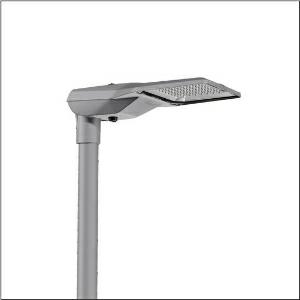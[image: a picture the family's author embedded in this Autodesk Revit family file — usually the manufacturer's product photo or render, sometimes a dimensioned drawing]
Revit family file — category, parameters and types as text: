
# Revit family: streetlight_sl_21_iq_midi___st1_0a_5xe3d61y08nb_32be
name_source: partatom
category: Lighting Fixtures
units: mm (PartAtom-declared; Revit-internal decimal feet)

## family parameters
Cut with Voids When Loaded = No
Host = Face
Light Source = No
Part Type = Normal
Room Calculation Point = No
Round Connector Dimension = Use Diameter
Shared = No

## types (1)
- --- (1 x LED, 18700 lm, 136.6 W, 2700K)
    Apparent Load = 137 VA
    CIE Flux Codes = 40 73 97 100 100
    Color Rendering = 70
    Color Temperature = 2700K
    Default Elevation = 1800 mm
    Description = Streetlight SL 21 iQ midi, mast luminaire, primary light control with lens, of PMMA, primary optical cover: cover, of toughened safety glass, transparent, light distribution: ST1.0a, light emission: direct distribution, primary light characteristic: asymmetric, installation type: post-top, side-entry, LED, High Power LED, rated luminous flux: 18.700lm, luminous efficacy: 137lm/W, light colour: 727, colour temperature: 2700K, control gear: iQ-Street Remote, D4i with power reduction, control: pre-setting: logarithmic dimming characteristic, Street-Remote, Auto-Match, Temp-Guard, Lumen-Switch, Night-Set, Smart-Wire, Light-Fading, Desk-Remote (wireless, voltage-free reading and setting of iQ features in the workshop via application-optimized NFC function/RFID function), optimised constant luminous flux control (CLO 2.0), mains connection: 230..240V, AC, 50/60Hz, start of lifetime: 137W, end of service life: 144W, reduction: 61W, luminaire housing, of diecast aluminium, powder-coated, Siteco® metallic grey (DB 702S), corrosivity category C5 mid according to DIN EN ISO 12944, please order mast flange separately, inclination adjustable: 0°, 5°, 10°, 15°, sealing non-destructively replaceable, multi-level sealing system, length: 644mm, width: 335mm, height: 110mm, mast flange for spigot size: 42mm (side-entry): 5XC10008XM4, 60/48mm (side-entry/post-top): 5XC10108XM2, 76/60mm (side-entry/post-top): 5XC10108XM1, mounting height: 4..8m, Smart Interface below and above, protection rating (complete): IP66, insulation class (complete): insulation class II (safety insulation), certification: CE, ENEC, ENEC+, VDE, impact resistance: IK10, permissible operating ambient temperature for outdoor applications: -40..+50°C, standard-compliant lighting for roads and squares, packaging unit: 1 piece

Light Distribution: ST1.0a
    Height = 111 mm
    Lamp = 1 x LED
    Lamp Light Flux = 18700 lm
    Lamp Power = 136.6 W
    Lamp count = 1
    Length = 644 mm
    Luminous efficacy = 137 lm/W
    Manufacturer = Siteco
    ModVariant = No
    Model = 5XE3D61Y08NB
    Number of Poles = 1
    OnlyDefault = Yes
    Power Factor = 1
    Product Name = Streetlight SL 21 iQ midi | ST1.0a
    Product group = mast luminaire | pylon top
    ProductGroupID = 6100
    Protection Class = Protection class II
    Protection Degree = IP 66
    RLX_Detail_Level = 1
    RLX_Emergency_Light_Flux = 0 lm
    RLX_Emergency_Type = 0
    RLX_Emergency_Type_DB = No
    RlxData = <blob elided: 90921 chars, md5=063e7b31>
    Socket = socket
    Standby Power = 0 W
    System Light Flux = 18701 lm
    System Power = 137 W
    Type Comments = factory setting: luminous flux: 100 % | dim-lin: 254 | 733 mA
    Type Image = l_1004304.jpg
    URL = http://relux.com
    VarID = @adj_135321
    Voltage = 0 V
    Weight = 0.00 kg
    Width = 336 mm

## geometry (parser evidence)
native form markers: Blend x4, Sweep x11
no freeform markers — native parametric forms only
